# Revit family: IS_Tesi_T3512_BIM_IT
name_source: partatom
category: Plumbing Fixtures
revit_build: Autodesk Revit MEP 2014 (Build: 20130308_1515(x64)
units: mm (PartAtom-declared; Revit-internal decimal feet)

## types (1)
- T351201 - TESI BASIN 70 WHITE BOXED
    Accessori = www.idealstandard.it
    AltezzaNominale = 212 mm
    Assembly Code = C1030200
    Autore = Ideal Standard Italia
    Brand = Ideal Standard
    CWFU = 0
    Caratteristiche = Lavabo da 700 mm dotato di foro centrale aperto per la rubinetteria. Può essere installato in abbinamento alla semicolonna o al sifone lineare cromato.
    CicloDiVitaDelProdotto = 0
    CodiceABarre = 8014140430179
    Colore = Bianco
    Connessione = Installazione
    Cost = 0 $
    CostoDiSostituzione = 0 $
    Default Elevation = 0 mm  [stored 0 ft]
    Description = Tesi basin 70 white boxed
    DescrizioneClassifcazioneUni2015 = Wash basin systems
    Dimensione = 530 x 700 x 212 mm
    DimensioneScarico = 0
    DurataGaranziaProdotti = 99
    Finitura = Bianco
    Garanzia = Garanzia Idealstandard
    HWFU = 0
    IfcEsportaCome = IfcSanitaryTerminalType
    InformaziniGaranzia = www.idealstandard.it/garanzia.html
    InformazioniDiProdotto = www.idealstandard.it/prodotti/html
    InformazioniGaranzia = www.idealstandard.it/garanzia.html
    InstruzioniInstallazione = www.idealstandard.it/prodotti/html
    LarghezzaNominale = 700 mm
    LunghezzaNominale = 530 mm
    Materiale = Porcellana Vetrificata (Vitreous China)
    Model = T351201
    Nome = WashBasinSystems_Tesi_T351201_Ideal Standard
    NomeOggettoBim = ISI_IdealStandard_WashBasinSystems_Tesi_T351201
    NumeroDiModello = T351201
    PesoNetto = 19.70 Kg
    Produttore = www.idealstandard.it
    ProfonditàNominale = 530 mm
    RiferimentoClassificazioneUni2015 = Ss_40_15_75_94
    Spazio = interno
    Telefono = 800 652 290
    TipoEspotazioneIfc = WASHHANDBASINS
    URL = www.idealstandard.it
    UnitàDurata = anni
    UnitàDurataGaranzia = anni
    UnitàVolume = Litri
    VersioneClassificazioneUni2015 = Products v1.1
    WFU = 0

note: [stored X ft] marks values corroborated as IEEE doubles in the binary element streams (Revit-internal decimal feet)

## geometry (parser evidence)
native form markers: Sweep x1
no freeform markers — native parametric forms only
